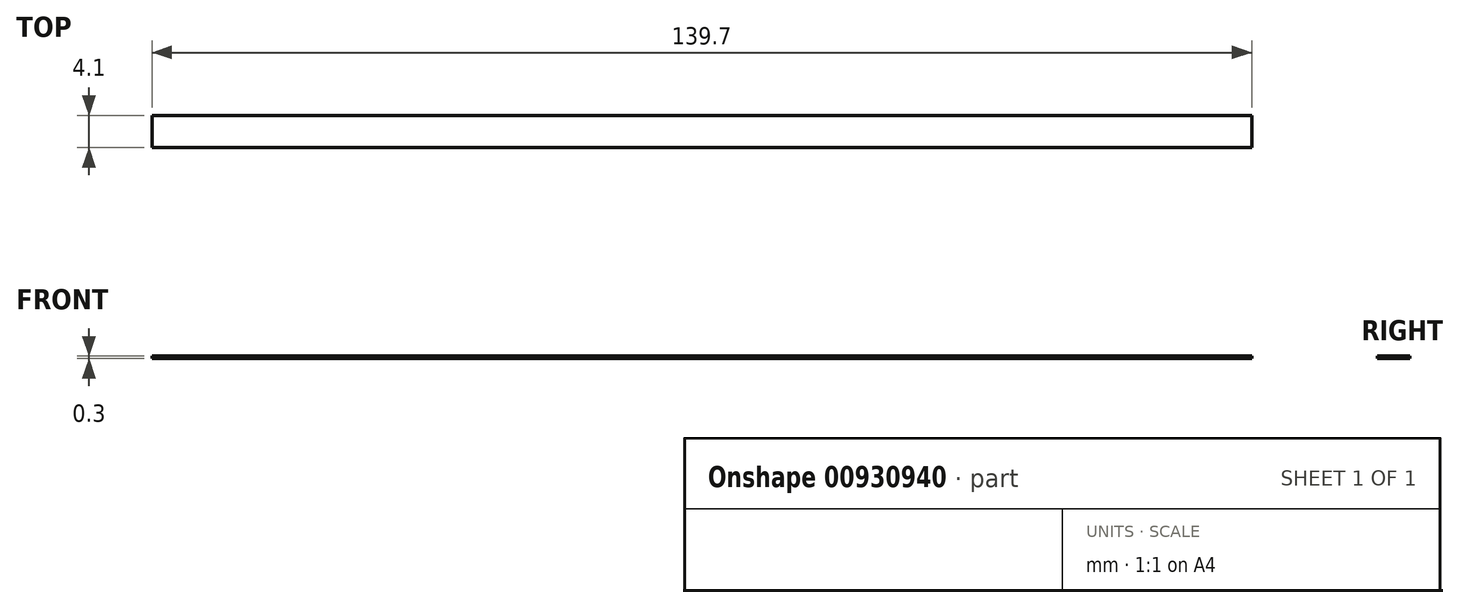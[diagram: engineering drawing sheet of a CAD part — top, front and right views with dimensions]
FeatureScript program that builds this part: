
annotation { "Feature Type Name" : "Feature", "Feature Type Description" : "" }
export const myFeature = defineFeature(function(context is Context, id is Id, definition is map)
    precondition{}
    {
        {
            var Q0;
            Q0=qCreatedBy(makeId("Top.planeOp"),FACE);
            var sketch = newSketch(context, id + "F0", { "sketchPlane" : qUnion([Q0])});
            skLineSegment(sketch, "E0.bottom", {"start": v(0, 0) * mm, "end": v(139.7, 0) * mm});
            skLineSegment(sketch, "E0.top", {"start": v(0, 4.1) * mm, "end": v(139.7, 4.1) * mm});
            skLineSegment(sketch, "E0.left", {"start": v(0, 0) * mm, "end": v(0, 4.1) * mm});
            skLineSegment(sketch, "E0.right", {"start": v(139.7, 0) * mm, "end": v(139.7, 4.1) * mm});
            skSolve(sketch);
        }
        {
            var Q0;
            Q0=makeQuery(id+"F0.imprint","IMPRINT",FACE,{"disambiguationData":[TD([[makeQuery(id+"F0.imprint","IMPRINT",EDGE,{"derivedFrom":sQuery(id+"F0.wireOp",EDGE,"E0.bottom")}),1.0]])]});
            extrude(context, id + "F1", {"entities" : qUnion([Q0]), "depth" : .3 * mm, "offsetDistance" : 25.4 * mm});
        }
    });
